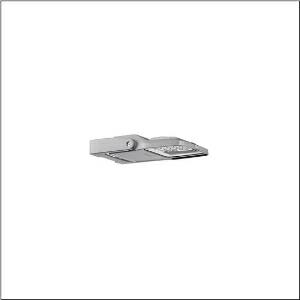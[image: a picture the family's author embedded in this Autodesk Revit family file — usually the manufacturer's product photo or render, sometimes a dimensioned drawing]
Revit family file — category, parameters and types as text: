
# Revit family: floodlight_fl_21_micro___pl43_5xa7761a2a2a_a8bd
name_source: partatom
category: Lighting Fixtures
units: mm (PartAtom-declared; Revit-internal decimal feet)

## family parameters
Cut with Voids When Loaded = No
Host = Face
Light Source = No
Part Type = Normal
Room Calculation Point = No
Round Connector Dimension = Use Diameter
Shared = No

## types (1)
- --- (1 x LED, 3040 lm, 23.1 W, 3000K)
    Apparent Load = 23 VA
    CIE Flux Codes = 29 80 99 100 100
    Color Rendering = 70
    Color Temperature = 3000K
    Default Elevation = 1800 mm
    Description = Floodlight FL 21 micro, floodlight, primary light control with lens, of PMMA, primary optical cover: protective disc, of toughened safety glass, transparent, light distribution: PL43, light emission: direct distribution, installation type: surface-mounted, LED, High Power LED, rated luminous flux: 3.040lm, luminous efficacy: 132lm/W, light colour: 730, colour temperature: 3000K, control gear: ECG iQ, control: optimised constant luminous flux control (CLO 2.0), Desk-Remote (wireless, voltage-free reading and setting of iQ features in the workshop via application-optimized NFC function/RFID function), Light-Fading, Smart-Wire, Night-Set, Lumen-Switch, Temp-Guard, Auto-Match, with terminal, 6-pole, mains connection: 220..240V, AC, 50/60Hz, start of lifetime: 23W, end of lifetime: 24W, reduction: 11W, luminaire housing, of diecast aluminium, powder-coated, Siteco® metallic grey (DB 702S), corrosivity category C5 according to DIN EN ISO 12944, design bracket, of diecast aluminium, powder-coated, Siteco® metallic grey (DB 702S), protection rating (complete): IP66, insulation class (complete): insulation class II (safety insulation), certification: CE, protection symbol: D, impact resistance: IK07, permissible operating ambient temperature: -40..+40°C, permissible operating ambient temperature for outdoor applications: -40..+50°C, standard: DIN EN 12944, packaging unit: 1 piece

Light Distribution: PL43
    Height = 65 mm
    Lamp = 1 x LED
    Lamp Light Flux = 3040 lm
    Lamp Power = 23.1 W
    Lamp count = 1
    Length = 312 mm
    Luminous efficacy = 132 lm/W
    Manufacturer = Siteco
    ModVariant = No
    Model = 5XA7761A2A2A
    Number of Poles = 1
    OnlyDefault = Yes
    Power Factor = 1
    Product Name = Floodlight FL 21 micro | PL43
    Product group = floodlight | pylon top
    ProductGroupID = 6101
    Protection Class = Protection class II
    Protection Degree = IP 66
    RLX_Detail_Level = 1
    RlxData = <blob elided: 97157 chars, md5=6d6bb93c>
    Socket = socket
    Standby Power = 0 W
    System Light Flux = 3040 lm
    System Power = 23 W
    Type Comments = factory setting: luminous flux: 100 % | dim-lin: 254 | 455 mA
    Type Image = l_1006878.jpg
    URL = http://relux.com
    VarID = @adj_090145
    Voltage = 0 V
    Weight = 0.00 kg
    Width = 230 mm

## geometry (parser evidence)
native form markers: Blend x4, Sweep x12
no freeform markers — native parametric forms only
